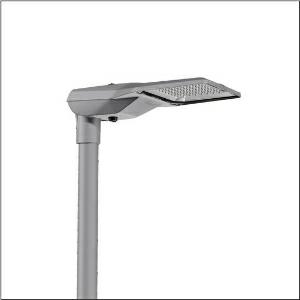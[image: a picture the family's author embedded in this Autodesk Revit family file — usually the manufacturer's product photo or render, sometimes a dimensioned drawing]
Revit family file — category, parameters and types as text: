
# Revit family: streetlight_sl_21_midi___st0_8a_5xe3c43t08nb_aee1
name_source: partatom
category: Lighting Fixtures
units: mm (PartAtom-declared; Revit-internal decimal feet)

## family parameters
Cut with Voids When Loaded = No
Host = Face
Light Source = No
Part Type = Normal
Room Calculation Point = No
Round Connector Dimension = Use Diameter
Shared = No

## types (1)
- --- (1 x LED, 23710 lm, 151.2 W, 4000K)
    Apparent Load = 151 VA
    CIE Flux Codes = 41 75 97 100 100
    Color Rendering = 70
    Color Temperature = 4000K
    Default Elevation = 1800 mm
    Description = Streetlight SL 21 midi, mast luminaire, primary light control with lens, of PMMA, primary optical cover: cover, of toughened safety glass, transparent, light distribution: ST0.8a, light emission: direct distribution, primary light characteristic: asymmetric, installation type: side-entry, post-top, LED, High Power LED, rated luminous flux: 23.710lm, luminous efficacy: 157lm/W, light colour: 740, colour temperature: 4000K, control gear: D4i, control: overheat protection, constant luminous flux control, time-dependent luminous flux control, flexible luminous flux parameterisation, pre-setting: logarithmic dimming characteristic, mains connection: 230..240V, AC, 50/60Hz, start of lifetime: 151W, end of service life: 157W, reduction: 70W, luminaire housing, of diecast aluminium, powder-coated, Siteco® metallic grey (DB 702S), corrosivity category C5 mid according to DIN EN ISO 12944, please order mast flange separately, inclination adjustable: 0°, 5°, 10°, 15°, sealing non-destructively replaceable, multi-level sealing system, length: 644mm, width: 335mm, height: 110mm, mast flange for spigot size: 42mm (side-entry): 5XC10008XM4, 60/48mm (side-entry/post-top): 5XC10108XM2, 76/60mm (side-entry/post-top): 5XC10108XM1, mounting height: 4..8m, Smart Interface below and above, protection rating (complete): IP66, insulation class (complete): insulation class II (safety insulation), certification: CE, ENEC, ENEC+, VDE, impact resistance: IK10, permissible operating ambient temperature for outdoor applications: -40..+50°C, standard-compliant lighting for roads and squares, packaging unit: 1 piece

Light Distribution: ST0.8a
    Height = 111 mm
    Lamp = 1 x LED
    Lamp Light Flux = 23710 lm
    Lamp Power = 151.2 W
    Lamp count = 1
    Length = 644 mm
    Luminous efficacy = 157 lm/W
    Manufacturer = Siteco
    ModVariant = No
    Model = 5XE3C43T08NB
    Number of Poles = 1
    OnlyDefault = Yes
    Power Factor = 1
    Product Name = Streetlight SL 21 midi | ST0.8a
    Product group = mast luminaire | pylon top
    ProductGroupID = 6100
    Protection Class = Protection class II
    Protection Degree = IP 66
    RLX_Detail_Level = 1
    RLX_Emergency_Light_Flux = 0 lm
    RLX_Emergency_Type = 0
    RLX_Emergency_Type_DB = No
    RlxData = <blob elided: 27025 chars, md5=519ac09b>
    Socket = socket
    Standby Power = 0 W
    System Light Flux = 23710 lm
    System Power = 151 W
    Type Comments = factory setting: luminous flux: 100 % | dim-lin: 254 | 802 mA
    Type Image = l_1004304.jpg
    URL = http://relux.com
    VarID = @adj_168606
    Voltage = 0 V
    Weight = 0.00 kg
    Width = 336 mm

## geometry (parser evidence)
native form markers: Blend x4, Sweep x10
no freeform markers — native parametric forms only
